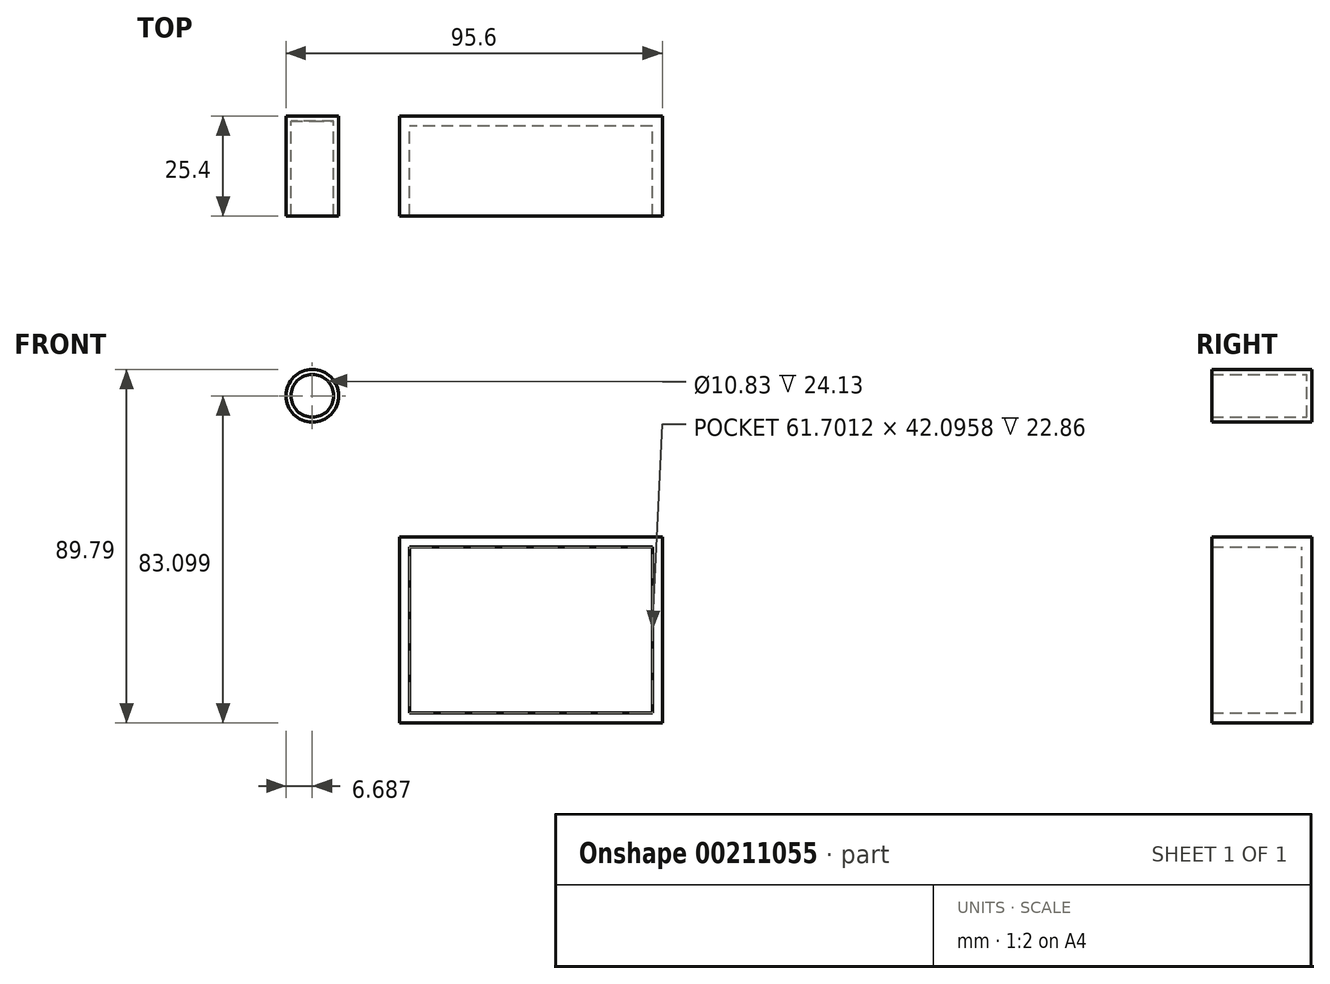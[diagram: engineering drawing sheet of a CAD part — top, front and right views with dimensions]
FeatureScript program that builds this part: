
annotation { "Feature Type Name" : "Feature", "Feature Type Description" : "" }
export const myFeature = defineFeature(function(context is Context, id is Id, definition is map)
    precondition{}
    {
        {
            var Q0;
            Q0=qCreatedBy(makeId("Front.planeOp"),FACE);
            var sketch = newSketch(context, id + "F0", { "sketchPlane" : qUnion([Q0])});
            skLineSegment(sketch, "E0.bottom", {"start": v(33.4, -23.59) * mm, "end": v(-33.4, -23.59) * mm});
            skLineSegment(sketch, "E0.top", {"start": v(33.4, 23.59) * mm, "end": v(-33.4, 23.59) * mm});
            skLineSegment(sketch, "E0.left", {"start": v(33.4, -23.59) * mm, "end": v(33.4, 23.59) * mm});
            skLineSegment(sketch, "E0.right", {"start": v(-33.4, -23.59) * mm, "end": v(-33.4, 23.59) * mm});
            skPoint(sketch, "E0.middle", {"position": v(0, 0) * mm});
            skSolve(sketch);
        }
        {
            var Q0;
            Q0 = qSketchRegion(id + "F0", true);
            extrude(context, id + "F1", {"entities" : qUnion([Q0]), "depth" : 25.4 * mm});
        }
        {
            var Q0;
            Q0=makeQuery(id+"F1.opExtrude","CAP_FACE",FACE,{"disambiguationData":[OSD([sQuery(id+"F0.wireOp",EDGE,"E0.bottom"),sQuery(id+"F0.wireOp",EDGE,"E0.top"),sQuery(id+"F0.wireOp",EDGE,"E0.left"),sQuery(id+"F0.wireOp",EDGE,"E0.right")])],"isStart":false});
            shell(context, id + "F2", {"entities" : qUnion([Q0]), "thickness" : 2.54 * mm});
        }
        {
            var Q0;
            Q0=qCreatedBy(makeId("Front.planeOp"),FACE);
            var sketch = newSketch(context, id + "F3", { "sketchPlane" : qUnion([Q0])});
            skCircle(sketch, "E1", {"center": v(-55.52, 59.5) * mm, "radius": 6.69 * mm});
            skSolve(sketch);
        }
        {
            var Q0;
            Q0 = qSketchRegion(id + "F3", true);
            extrude(context, id + "F4", {"entities" : qUnion([Q0]), "depth" : 25.4 * mm});
        }
        {
            var Q0;
            Q0=makeQuery(id+"F4.opExtrude","CAP_FACE",FACE,{"disambiguationData":[OSD([sQuery(id+"F3.wireOp",EDGE,"E1")])],"isStart":false});
            shell(context, id + "F5", {"entities" : qUnion([Q0]), "thickness" : 1.27 * mm});
        }
    });
